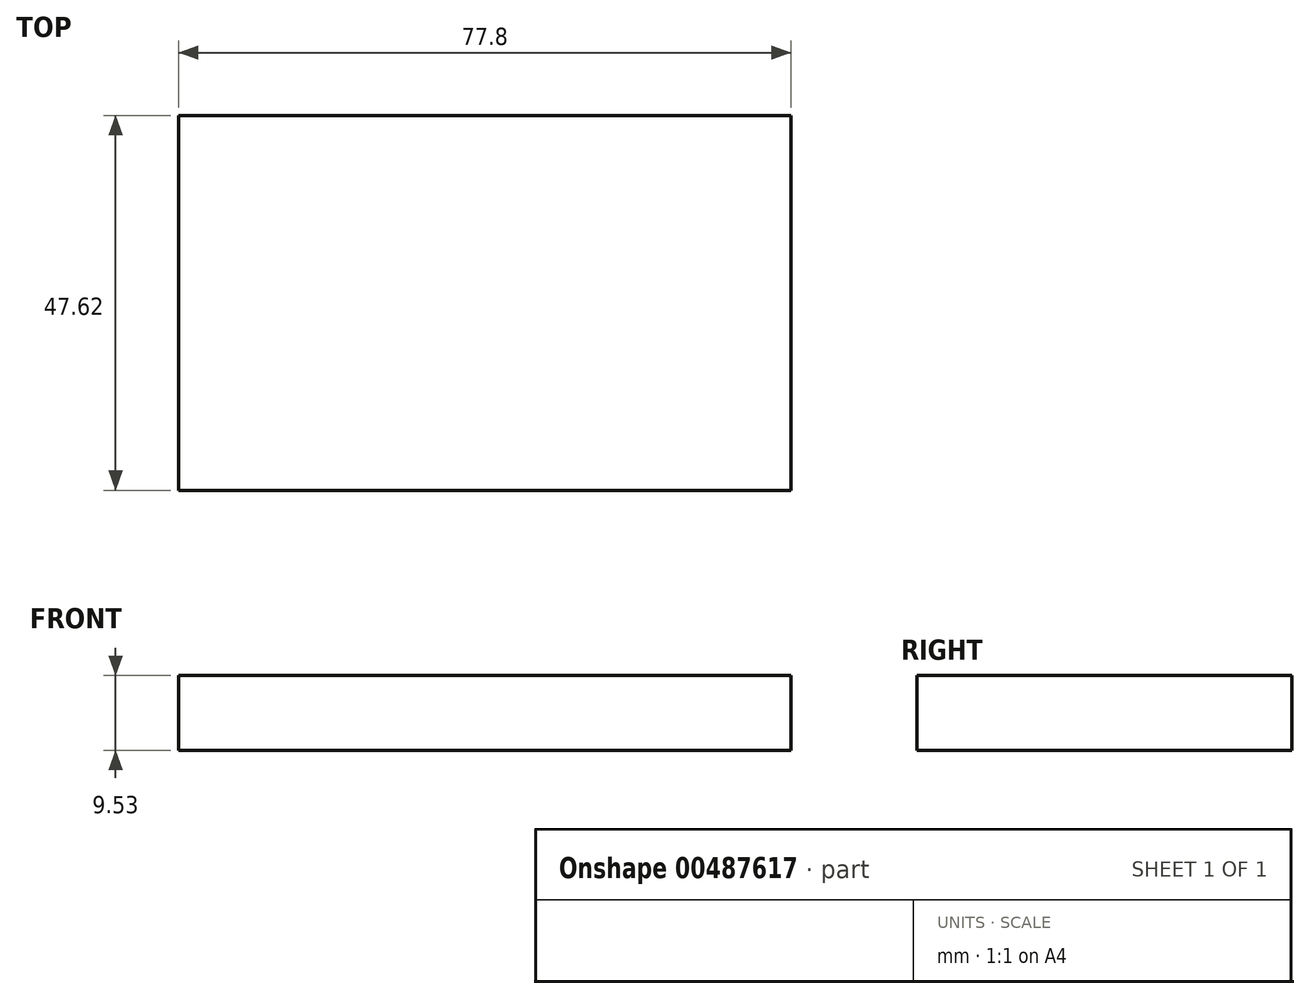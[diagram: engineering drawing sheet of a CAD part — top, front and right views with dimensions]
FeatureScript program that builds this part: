
annotation { "Feature Type Name" : "Feature", "Feature Type Description" : "" }
export const myFeature = defineFeature(function(context is Context, id is Id, definition is map)
    precondition{}
    {
        {
            var Q0;
            Q0=qCreatedBy(makeId("Top.planeOp"),FACE);
            var sketch = newSketch(context, id + "F0", { "sketchPlane" : qUnion([Q0])});
            skLineSegment(sketch, "E0.bottom", {"start": v(-38.9, 23.81) * mm, "end": v(38.9, 23.81) * mm});
            skLineSegment(sketch, "E0.top", {"start": v(-38.9, -23.81) * mm, "end": v(38.9, -23.81) * mm});
            skLineSegment(sketch, "E0.left", {"start": v(-38.9, 23.81) * mm, "end": v(-38.9, -23.81) * mm});
            skLineSegment(sketch, "E0.right", {"start": v(38.9, 23.81) * mm, "end": v(38.9, -23.81) * mm});
            skPoint(sketch, "E0.middle", {"position": v(0, 0) * mm});
            skSolve(sketch);
        }
        {
            var Q0;
            Q0 = qSketchRegion(id + "F0", true);
            extrude(context, id + "F1", {"entities" : qUnion([Q0]), "depth" : 9.52 * mm});
        }
    });
